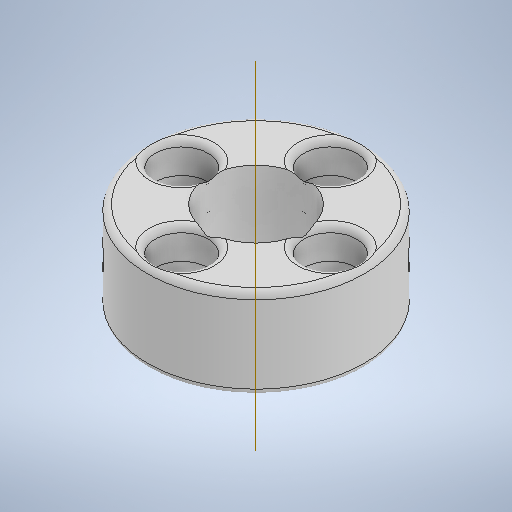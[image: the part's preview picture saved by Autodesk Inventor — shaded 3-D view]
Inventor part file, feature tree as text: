
AUTODESK INVENTOR PART (.ipt)
format: ipt  version: 2025.1 (Build 291241000, 241)  size: 395,776 bytes
history: native  units: mm
features: extrude x4, sketch x4, other x3, fillet x1
ambient origin geometry x8: Origin, YZ Plane, XZ Plane, XY Plane, X Axis, Y Axis, Z Axis, Center Point
bodies: Solide1 (feature_tree)
feature tree (12):
  extrude  "Extrusion1"  Depth=35.0mm
  extrude  "Extrusion2"  Depth=24.0mm
  extrude  "Extrusion3"  Depth=4.0mm
  fillet  "Congé2"  Radius=14.5mm
  other  "Plan de construction3"
  extrude  "Extrusion5"  Depth=40.0mm TaperAngle=360.0deg
  sketch  "Esquisse1"
  sketch  "Esquisse2"
  other  "Réseau d'esquisse circulaire2"
  other  "Réseau d'esquisse circulaire3"
  sketch  "Esquisse3"
  sketch  "Esquisse7"
